# Revit family: Magnus Adjustable 2x - 4000K (Narrow)
name_source: partatom
category: Lighting Fixtures
units: mm (PartAtom-declared; Revit-internal decimal feet)

## family parameters
Always vertical = Yes
Cut with Voids When Loaded = No
Host = Ceiling
Light Source = No
OmniClass Number = 23.80.70.11
OmniClass Title = Luminaries for Internal Lighting
Part Type = Normal
Room Calculation Point = No
Round Connector Dimension = Use Diameter
Shared = No

## types (1)
- Type 1
    Beam Angle Degree = 33.6
    Bining = ≤3SDCM
    CCT(K) = 4000
    CRI = 90
    Certification = Available on request
    Colors = Metalic Chrome, Black, White
    Default Elevation = 0 mm  [stored 0 ft]
    Driver Type = On-Off/ Dali 2.0/ DT8.0/ BLE/AD/ TD
    Driving Current( mA) = 350
    Efficacy (Lm/W) = 82.83
    Efficiency = >92 %
    IP Rating = IP20
    Lamp Flux( lm) = 792.342
    Lifetime = L80/B10(>50,000hrs@Ta-30Deg C)
    Manufacturer = pluslighttech.
    THD = <10%
    Tilt Angle = 30.00°
    Tuneable & Dimmable = Yes
    UGR = <10
    URL = https://pluslighttech.com
    Wattage(W) = 10
    Weight = 0 mm  [stored 0 ft]

note: [stored X ft] marks values corroborated as IEEE doubles in the binary element streams (Revit-internal decimal feet)

## geometry (parser evidence)
native form markers: Sweep x213
no freeform markers — native parametric forms only
